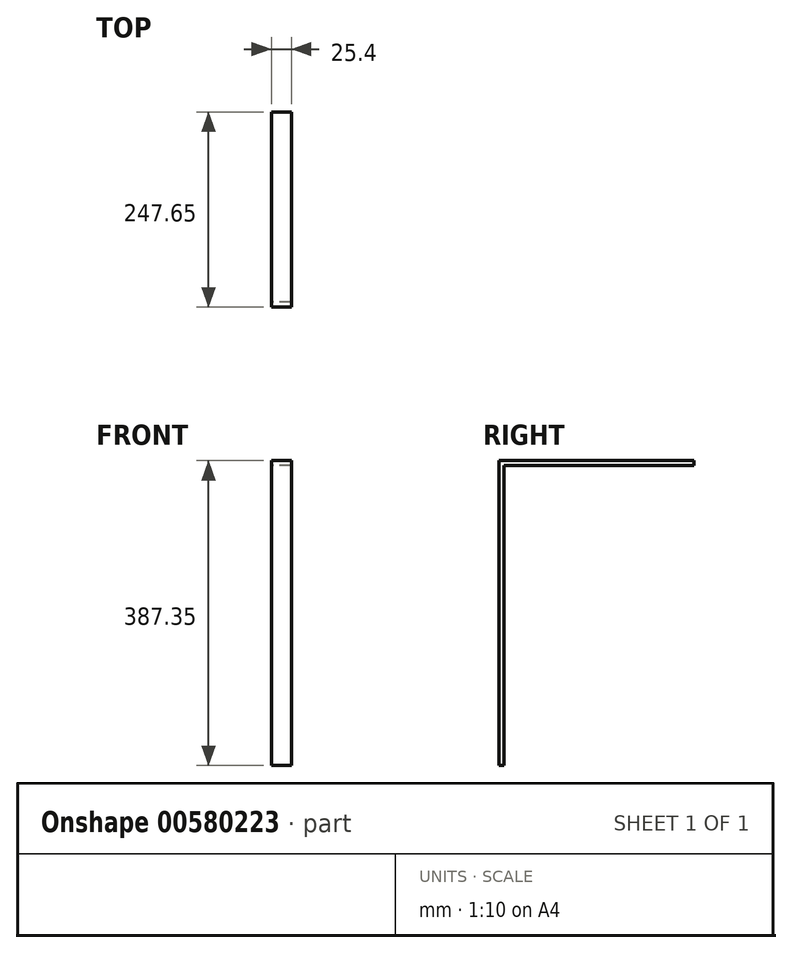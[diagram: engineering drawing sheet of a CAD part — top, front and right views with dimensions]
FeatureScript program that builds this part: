
annotation { "Feature Type Name" : "Feature", "Feature Type Description" : "" }
export const myFeature = defineFeature(function(context is Context, id is Id, definition is map)
    precondition{}
    {
        {
            var Q0;
            Q0=qCreatedBy(makeId("Right.planeOp"),FACE);
            var sketch = newSketch(context, id + "F0", { "sketchPlane" : qUnion([Q0])});
            skLineSegment(sketch, "E0", {"start": v(0, 0) * mm, "end": v(0, 387.35) * mm});
            skLineSegment(sketch, "E1", {"start": v(0, 387.35) * mm, "end": v(247.65, 387.35) * mm});
            skLineSegment(sketch, "E2", {"start": v(247.65, 387.35) * mm, "end": v(247.65, 381) * mm});
            skLineSegment(sketch, "E3", {"start": v(247.65, 381) * mm, "end": v(6.35, 381) * mm});
            skLineSegment(sketch, "E4", {"start": v(6.35, 381) * mm, "end": v(6.35, 0) * mm});
            skLineSegment(sketch, "E5", {"start": v(6.35, 0) * mm, "end": v(0, 0) * mm});
            skSolve(sketch);
        }
        {
            var Q0;
            Q0=makeQuery(id+"F0.imprint","IMPRINT",FACE,{"disambiguationData":[TD([[makeQuery(id+"F0.imprint","IMPRINT",EDGE,{"derivedFrom":sQuery(id+"F0.wireOp",EDGE,"E0")}),-1.0]])]});
            extrude(context, id + "F1", {"entities" : qUnion([Q0]), "depth" : 25.4 * mm, "offsetDistance" : 25.4 * mm});
        }
    });
